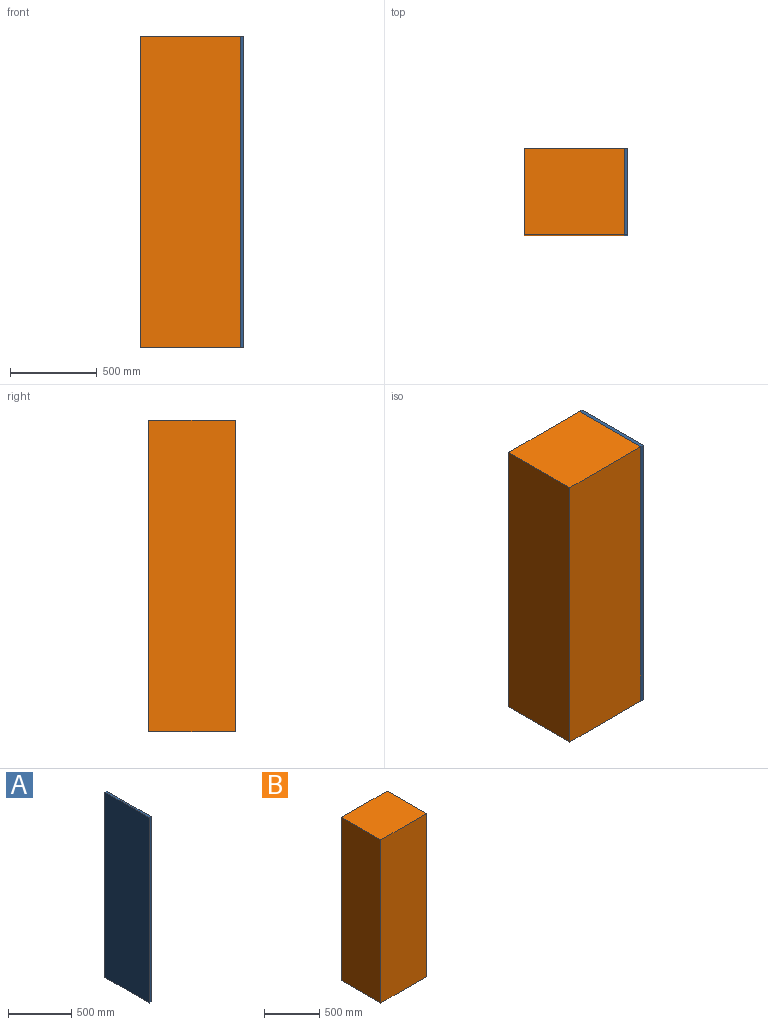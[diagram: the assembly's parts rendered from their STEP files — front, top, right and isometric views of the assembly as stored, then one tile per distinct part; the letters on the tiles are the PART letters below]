
ASSEMBLY  parts=2 mates=1
PART A: 6 faces, bbox 20x500x1800 mm
  f0: plane 500x20mm, normal (0,0,1), area 10000mm2, adj f1,f3,f4,f5
  f1: plane 1800x500mm, normal (-1,0,0), area 900000mm2, adj f0,f2,f3,f4
  f2: plane 500x20mm, normal (0,0,-1), area 10000mm2, adj f1,f3,f4,f5
  f3: plane 1800x20mm, normal (0,-1,0), area 36000mm2, adj f0,f1,f2,f5
  f4: plane 1800x20mm, normal (0,1,0), area 36000mm2, adj f0,f1,f2,f5
  f5: plane 1800x500mm, normal (1,0,0), area 900000mm2, adj f0,f2,f3,f4
PART B: 11 faces, bbox 580x500x1800 mm
  f0: plane 1800x500mm, normal (1,0,0), area 90400mm2, adj f1,f3,f4,f5,f6,f8,f9,f10
  f1: plane 1800x580mm, normal (0,1,0), area 1044000mm2, adj f0,f2,f4,f5
  f2: plane 1800x500mm, normal (-1,0,0), area 900000mm2, adj f1,f3,f4,f5
  f3: plane 1800x580mm, normal (0,-1,0), area 1044000mm2, adj f0,f2,f4,f5
  f4: plane 580x500mm, normal (0,0,1), area 290000mm2, adj f0,f1,f2,f3
  f5: plane 580x500mm, normal (0,0,-1), area 290000mm2, adj f0,f1,f2,f3
  f6: plane 1760x560mm, normal (0,-1,0), area 985600mm2, adj f0,f7,f9,f10
  f7: plane 1760x460mm, normal (1,0,0), area 809600mm2, adj f6,f8,f9,f10
  f8: plane 1760x560mm, normal (0,1,0), area 985600mm2, adj f0,f7,f9,f10
  f9: plane 560x460mm, normal (0,0,-1), area 257600mm2, adj f0,f6,f7,f8
  f10: plane 560x460mm, normal (0,0,1), area 257600mm2, adj f0,f6,f7,f8
PLACE A at identity
PLACE B at identity fixed
MATE revolute B.f4 <-> A.f0  axis (0,0,-1) through (580,500,1800)mm
